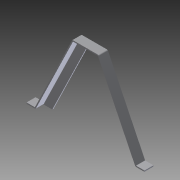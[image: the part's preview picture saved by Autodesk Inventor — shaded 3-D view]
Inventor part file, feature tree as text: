
AUTODESK INVENTOR PART (.ipt)
format: ipt  version: 2012 (Build 160160000, 160)  size: 133,120 bytes
history: native  units: in
note: dims shown in document units (in); Inventor stores cm internally (conversion verified against a paired STEP export)
features: extrude x2, fillet x2, sketch x1
ambient origin geometry x8: Origin, YZ Plane, XZ Plane, XY Plane, X Axis, Y Axis, Z Axis, Center Point
bodies: Solid1 (feature_tree)
feature tree (5):
  sketch  "Sketch1"  dims[d1=2.75in d4=0.125in d5=0.125in d10=1.0in d11=0.0in d12=0.125in d13=0.0in d14=0.0312in d15=0.125in d29=0.4013in d34=0.875in d35=1.0in d36=0.0625in d37=0.0625in d41=0.125in d43=8.625in d44=0.125in d45=0.4405in d46=0.4405in d47=0.125in d48=1.0in d49=1.0in d50=13.0in]
  extrude  "Extrusion1"  Depth=0.125in
  extrude  "Extrusion2"  Depth=0.125in
  fillet  "Fillet1"  Radius=1.0in
  fillet  "Fillet2"  Radius=0.125in
